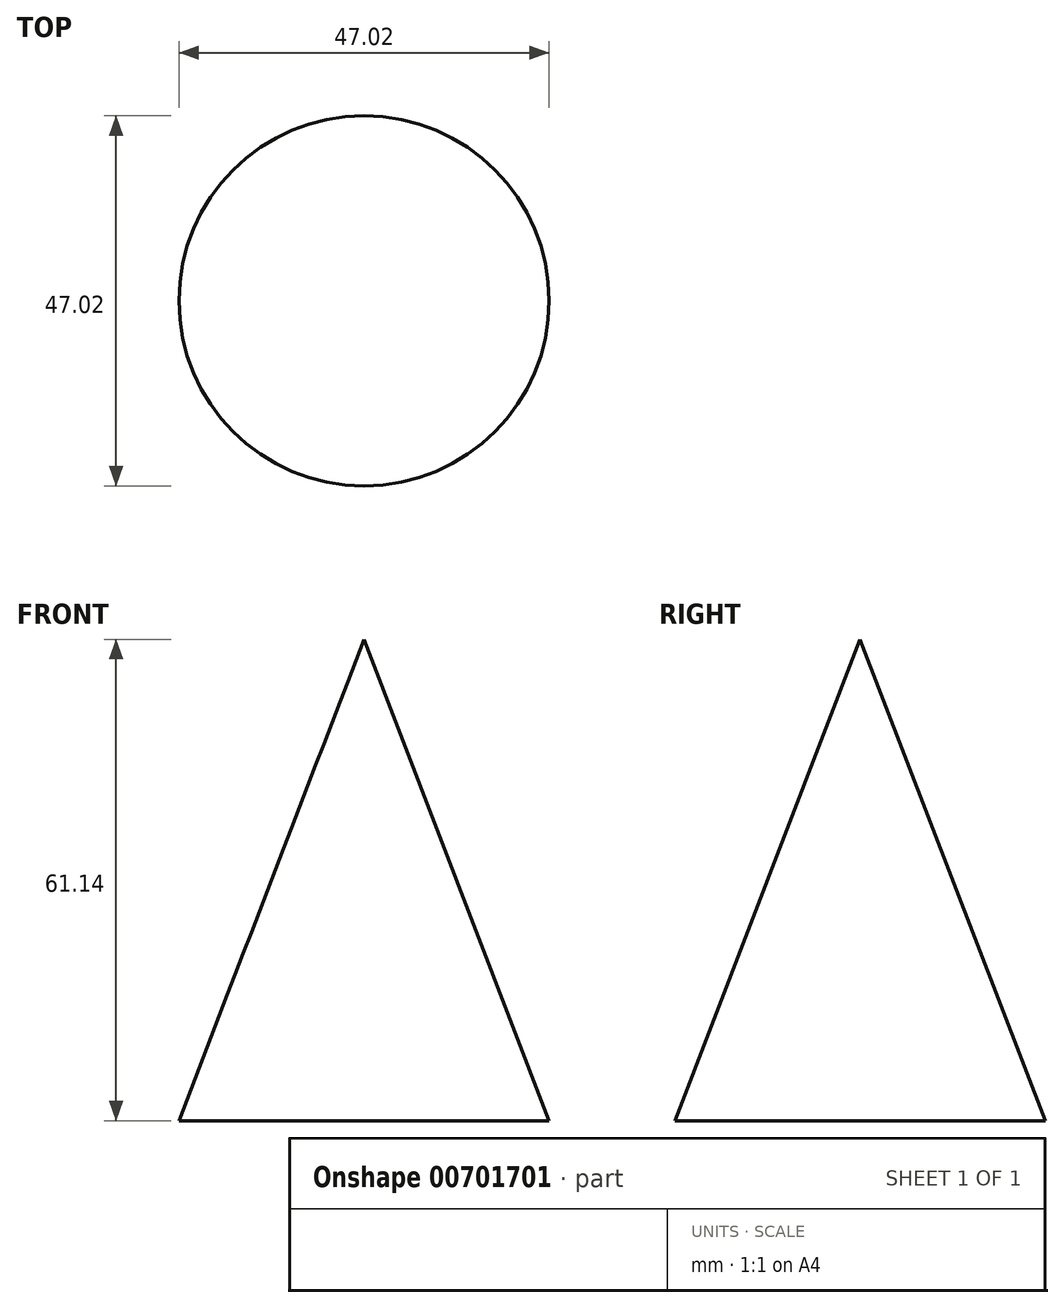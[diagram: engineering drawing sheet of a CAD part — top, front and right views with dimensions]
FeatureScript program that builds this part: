
annotation { "Feature Type Name" : "Feature", "Feature Type Description" : "" }
export const myFeature = defineFeature(function(context is Context, id is Id, definition is map)
    precondition{}
    {
        {
            var Q0;
            Q0=qCreatedBy(makeId("Front.planeOp"),FACE);
            var sketch = newSketch(context, id + "F0", { "sketchPlane" : qUnion([Q0])});
            skLineSegment(sketch, "E0", {"start": v(0, 0) * mm, "end": v(23.51, 0) * mm});
            skLineSegment(sketch, "E1", {"start": v(23.51, 0) * mm, "end": v(0, 61.14) * mm});
            skLineSegment(sketch, "E2", {"start": v(0, 61.14) * mm, "end": v(0, 0) * mm});
            skSolve(sketch);
        }
        {
            var Q0;
            Q0=makeQuery(id+"F0.imprint","IMPRINT",FACE,{"disambiguationData":[TD([[makeQuery(id+"F0.imprint","IMPRINT",EDGE,{"derivedFrom":sQuery(id+"F0.wireOp",EDGE,"E0")}),1.0]])]});
            var Q1;
            Q1=sQuery(id+"F0.wireOp",EDGE,"E2");
            revolve(context, id + "F1", {"entities" : qUnion([Q0]), "axis" : qUnion([Q1]), "revolveType" : RevolveType.FULL});
        }
    });
